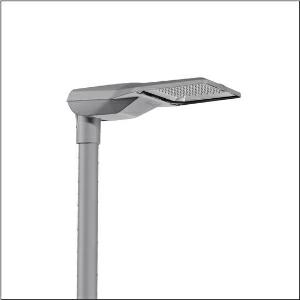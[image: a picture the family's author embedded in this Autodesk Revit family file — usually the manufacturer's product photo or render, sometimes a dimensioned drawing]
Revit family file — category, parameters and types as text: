
# Revit family: streetlight_sl_21_iq_midi___st1_0a_5xe3d31g08nb_2a13
name_source: partatom
category: Lighting Fixtures
units: mm (PartAtom-declared; Revit-internal decimal feet)

## family parameters
Cut with Voids When Loaded = No
Host = Face
Light Source = No
Part Type = Normal
Room Calculation Point = No
Round Connector Dimension = Use Diameter
Shared = No

## types (1)
- --- (1 x LED, 23230 lm, 155.5 W, 3000K)
    Apparent Load = 155 VA
    CIE Flux Codes = 40 73 97 100 100
    Color Rendering = 70
    Color Temperature = 3000K
    Default Elevation = 1800 mm
    Description = Streetlight SL 21 iQ midi, mast luminaire, primary light control with lens, of PMMA, primary optical cover: cover, of toughened safety glass, transparent, light distribution: ST1.0a, light emission: direct distribution, primary light characteristic: asymmetric, installation type: post-top, side-entry, LED, High Power LED, rated luminous flux: 23.230lm, luminous efficacy: 149lm/W, light colour: 730, colour temperature: 3000K, control: Street-Remote, Auto-Match, Temp-Guard, Lumen-Switch, Night-Set, Smart-Wire, Light-Fading, Desk-Remote (wireless, voltage-free reading and setting of iQ features in the workshop via application-optimized NFC function/RFID function), optimised constant luminous flux control (CLO 2.0), presetting dimming linear, mains connection: 230..240V, AC, 50/60Hz, start of lifetime: 156W, end of service life: 162W, reduction: 69W, luminaire housing, of diecast aluminium, powder-coated, Siteco® metallic grey (DB 702S), corrosivity category C5 mid according to DIN EN ISO 12944, please order mast flange separately, inclination adjustable: 0°, 5°, 10°, 15°, sealing non-destructively replaceable, multi-level sealing system, length: 644mm, width: 335mm, height: 110mm, mast flange for spigot size: 42mm (side-entry): 5XC10008XM4, 60/48mm (side-entry/post-top): 5XC10108XM2, 76/60mm (side-entry/post-top): 5XC10108XM1, protection rating (complete): IP66, insulation class (complete): insulation class II (safety insulation), certification: CE, ENEC, ENEC+, VDE, impact resistance: IK09, permissible operating ambient temperature for outdoor applications: -40..+50°C, standard-compliant lighting for roads and squares, packaging unit: 1 piece

Light Distribution: ST1.0a
    Height = 111 mm
    Lamp = 1 x LED
    Lamp Light Flux = 23230 lm
    Lamp Power = 155.5 W
    Lamp count = 1
    Length = 644 mm
    Luminous efficacy = 149 lm/W
    Manufacturer = Siteco
    ModVariant = No
    Model = 5XE3D31G08NB
    Number of Poles = 1
    OnlyDefault = Yes
    Power Factor = 1
    Product Name = Streetlight SL 21 iQ midi | ST1.0a
    Product group = mast luminaire | pylon top
    ProductGroupID = 6100
    Protection Class = Protection class II
    Protection Degree = IP 66
    RLX_Detail_Level = 1
    RLX_Emergency_Light_Flux = 0 lm
    RLX_Emergency_Type = 0
    RLX_Emergency_Type_DB = No
    RlxData = <blob elided: 90713 chars, md5=4eac8c5a>
    Socket = socket
    Standby Power = 0 W
    System Light Flux = 23230 lm
    System Power = 155 W
    Type Comments = factory setting: luminous flux: 100 % | dim-lin: 254 | 823 mA
    Type Image = l_1004298.jpg
    URL = http://relux.com
    VarID = @adj_103583
    Voltage = 0 V
    Weight = 0.00 kg
    Width = 336 mm

## geometry (parser evidence)
native form markers: Blend x4, Sweep x10
no freeform markers — native parametric forms only
